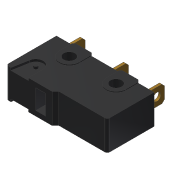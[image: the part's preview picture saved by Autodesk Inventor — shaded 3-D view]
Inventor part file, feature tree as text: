
AUTODESK INVENTOR PART (.ipt)
format: ipt  version: 2014 SP2 (Build 180247200, 247)  size: 326,656 bytes
history: native  units: mm
features: extrude x7, sketch x7, chamfer x3, mirror x3, hole x1, fillet x1
ambient origin geometry x8: Origin, YZ Plane, XZ Plane, XY Plane, X Axis, Y Axis, Z Axis, Center Point
bodies: Solid1 (feature_tree)
feature tree (22):
  extrude  "Extrusion1"  Depth=9.5mm
  chamfer  "Chamfer1"  Distance=10.0mm
  chamfer  "Chamfer3"  Distance=5.1mm
  extrude  "Extrusion2"  Depth=9.5mm
  mirror  "Mirror1"
  extrude  "Extrusion3"  Depth=2.0mm
  extrude  "Extrusion4"  Depth=2.0mm
  chamfer  "Chamfer2"  Distance=3.2mm
  hole  "Hole1"  [1 undecoded]
  extrude  "Extrusion5"  Depth=3.0mm
  extrude  "Extrusion6"  Depth=6.0mm TaperAngle=0.0deg
  mirror  "Mirror2"
  extrude  "Extrusion7"  Depth=0.4mm TaperAngle=45.0deg
  mirror  "Mirror3"
  fillet  "Fillet1"  Radius=4.0mm
  sketch  "Sketch2"  dims[d2=19.8mm d3=9.5mm]
  sketch  "Sketch3"  dims[d4=7.0mm]
  sketch  "Sketch4"  dims[d5=4.75mm]
  sketch  "Sketch6"  dims[d6=0.4mm]
  sketch  "Sketch7"  dims[d8=0.4mm]
  sketch  "Sketch8"  dims[d10=4.0mm]
  sketch  "Sketch9"  dims[d11=4.0mm d13=10.0mm d14=5.1mm d15=9.5mm d16=2.0mm d17=2.0mm d18=3.2mm d21=2.3mm d22=2.3mm d23=6.0mm d24=0.0mm d25=0.4mm d26=2.0mm d27=45.0deg d28=4.0mm d29=4.0mm d30=4.0mm d31=0.2mm d32=0.0mm d33=2.0mm d34=4.0mm d35=1.0mm d36=2.0mm d37=4.0mm d38=0.0mm d39=3.4mm d40=3.4mm d41=0.5mm d42=0.5mm d43=1.7mm d44=1.7mm d46=9.3mm d47=3.4mm d48=0.5mm d49=1.7mm d50=16.6mm d51=4.0mm d52=0.0mm d53=0.5mm d54=2.0mm d55=45.0deg d56=3.4mm d57=1.7mm d58=1.5mm d59=1.6mm d60=6.0mm d61=4.0mm d62=2.0mm d63=90.0deg d64=8.0mm d65=20.594885mm d66=3.0mm d68=3.0mm d69=3.0mm d70=0.5mm d71=0.0mm d72=0.8mm d73=0.5mm d74=0.0mm d75=1.745329mm d76=10.0mm d77=0.0mm d78=0.5mm d80=7.2mm d81=2.5mm d82=2.5mm d83=10.2mm d84=0.7mm d85=2.0mm d86=45.0deg d87=8.8mm d88=7.3mm d89=3.1mm d90=1.55mm d91=6.0mm d92=3.0mm]
note: 1 required parameter value undecoded (feature->parameter linkage not recoverable at this tier; creation-order binding heuristic only, values carry confidence <= 0.55)
